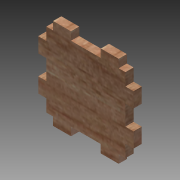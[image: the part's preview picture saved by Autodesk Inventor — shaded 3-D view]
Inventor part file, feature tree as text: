
AUTODESK INVENTOR PART (.ipt)
format: ipt  version: 2015 (Build 190159000, 159)  size: 441,344 bytes
history: native  units: mm
features: other x13, sketch x9, extrude x4
ambient origin geometry x8: Origin, YZ Plane, XZ Plane, XY Plane, X Axis, Y Axis, Z Axis, Center Point
bodies: Solid1 (feature_tree)
feature tree (26):
  other  "Blocks"
  extrude  "Extrusion1"  Depth=50.0mm
  extrude  "Extrusion3"  TaperAngle=0.0deg  [1 undecoded]
  extrude  "Extrusion10"  Depth=20.0mm
  extrude  "Extrusion11"  Depth=5.5mm
  sketch  "Sketch20"  dims[d48=8.333333mm]
  sketch  "Sketch21"  dims[d49=5.5mm d50=0.0mm d51=5.5mm d53=5.5mm d54=10.0mm d55=5.5mm d56=0.0mm d58=0.1mm d60=0.1mm d61=0.1mm d64=0.1mm d65=0.1mm d66=0.1mm d67=0.1mm d76=0.08mm]
  sketch  "Sketch19"  dims[d47=5.5mm]
  sketch  "Sketch17"  dims[d13=0.0mm]
  sketch  "Sketch18"  dims[d37=5.5mm]
  sketch  "Sketch2"  dims[d0=64.0mm d1=50.0mm]
  sketch  "Sketch4"  dims[d2=5.5mm d3=0.0mm]
  sketch  "Sketch7"  dims[d9=5.5mm d10=20.0mm]
  other  "Block1"
  sketch  "Sketch8"  dims[d11=12.0mm d12=5.5mm]
  other  "Block2"
  other  "Block3"
  other  "Block4"
  other  "Block5"
  other  "Block6"
  other  "Block7"
  other  "Block8"
  other  "Block7:1"
  other  "Block7:2"
  other  "Block8:1"
  other  "Block8:2"
note: 1 required parameter value undecoded (feature->parameter linkage not recoverable at this tier; creation-order binding heuristic only, values carry confidence <= 0.55)
